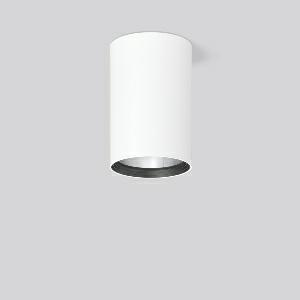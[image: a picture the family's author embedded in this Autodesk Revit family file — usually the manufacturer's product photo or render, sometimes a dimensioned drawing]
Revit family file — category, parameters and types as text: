
# Revit family: heledon_maxi_a_931224_002_2_ad57
name_source: partatom
category: Lighting Fixtures
units: mm (PartAtom-declared; Revit-internal decimal feet)

## family parameters
Cut with Voids When Loaded = No
Host = Face
Light Source = No
Part Type = Normal
Room Calculation Point = No
Round Connector Dimension = Use Diameter
Shared = No

## types (1)
- HELEDON maxi A (1 x LED Modul 927, 4100 lm, 2700)
    Apparent Load = 35 VA
    Approval mark = CE
    CIE Flux Codes = 100 100 100 100 100
    Color Rendering = 92
    Color Temperature = 2700
    Default Elevation = 1800 mm
    Description = Series: HELEDON maxi
Cylindrical surface-mounted downlight. Housing: die-cast aluminium, powder-coated. Internal ceiling frame polycarbonate with bayonet mounting. Black plastic ring and recessed LED to prevent glare from the side. Optical assembly with reflector made of MIRO-Silver with 98% total light reflection for outstanding efficiency - can be changed without tools. Best colour rendering index Ra>90. Suitable for Ceiling mounting. Easy installation with a separate ceiling frame with bayonet mounting and plug connection. Driver integrated. Connected via plug-in connector. High quality converter without flickering and stroboscopic effect. The following accessories can be mounted without use of tools: interchangeable lenses, decorative glasses, honeycomb louvre, clear and frosted diffusers, white interchangeable plastic ring. 
Colour: traffic white, matt (RAL 9016)
Diameter: 123 mm
Height: 183 mm
Lamp: LED
Socket: without socket
Colour temperature: 2700K
Colour rendering index (CRI): 92
System power: 35 W
Rated luminous flux: 4100 lm
Luminous efficiency: 117 lm/W
Control gear: Regulated power supply
Protection class: I
Type of protection: IP 20
    Height = 183 mm
    Lamp = 1 x LED Modul 927
    Lamp Light Flux = 4100 lm
    Lamp count = 1
    Length = 123 mm
    Lifetime = 50000 h
    Luminous efficacy = 117 lm/W
    Manufacturer = RZB
    ModVariant = No
    Model = 931224.002.2
    Mounting Place = Ceiling
    Mounting Type = Surface mounted
    Number of Poles = 1
    OnlyDefault = Yes
    Power Factor = 1
    Product Name = HELEDON maxi A
    Product group = Surface mounted downlights
    ProductGroupID = 302
    Protection Class = Protection class I
    Protection Degree = IP 20
    RLX_Detail_Level = 1
    RLX_Emergency_Light_Flux = 0 lm
    RLX_Emergency_Type = 0
    RLX_Emergency_Type_DB = No
    RlxData = <blob elided: 98341 chars, md5=150f1725>
    Socket = socket
    Standby Power = 0 W
    System Light Flux = 4100 lm
    System Power = 35 W
    Type Comments = Product without accessories
    Type Image = 931192.002.jpg
    URL = http://relux.com
    VarID = ---
    Voltage = 230 V
    Voltage Range = 220-240 V
    Weight = 0.00 kg
    Width = 0 mm  [stored 0 ft]

note: [stored X ft] marks values corroborated as IEEE doubles in the binary element streams (Revit-internal decimal feet)

## geometry (parser evidence)
native form markers: Blend x4, Sweep x10
no freeform markers — native parametric forms only
